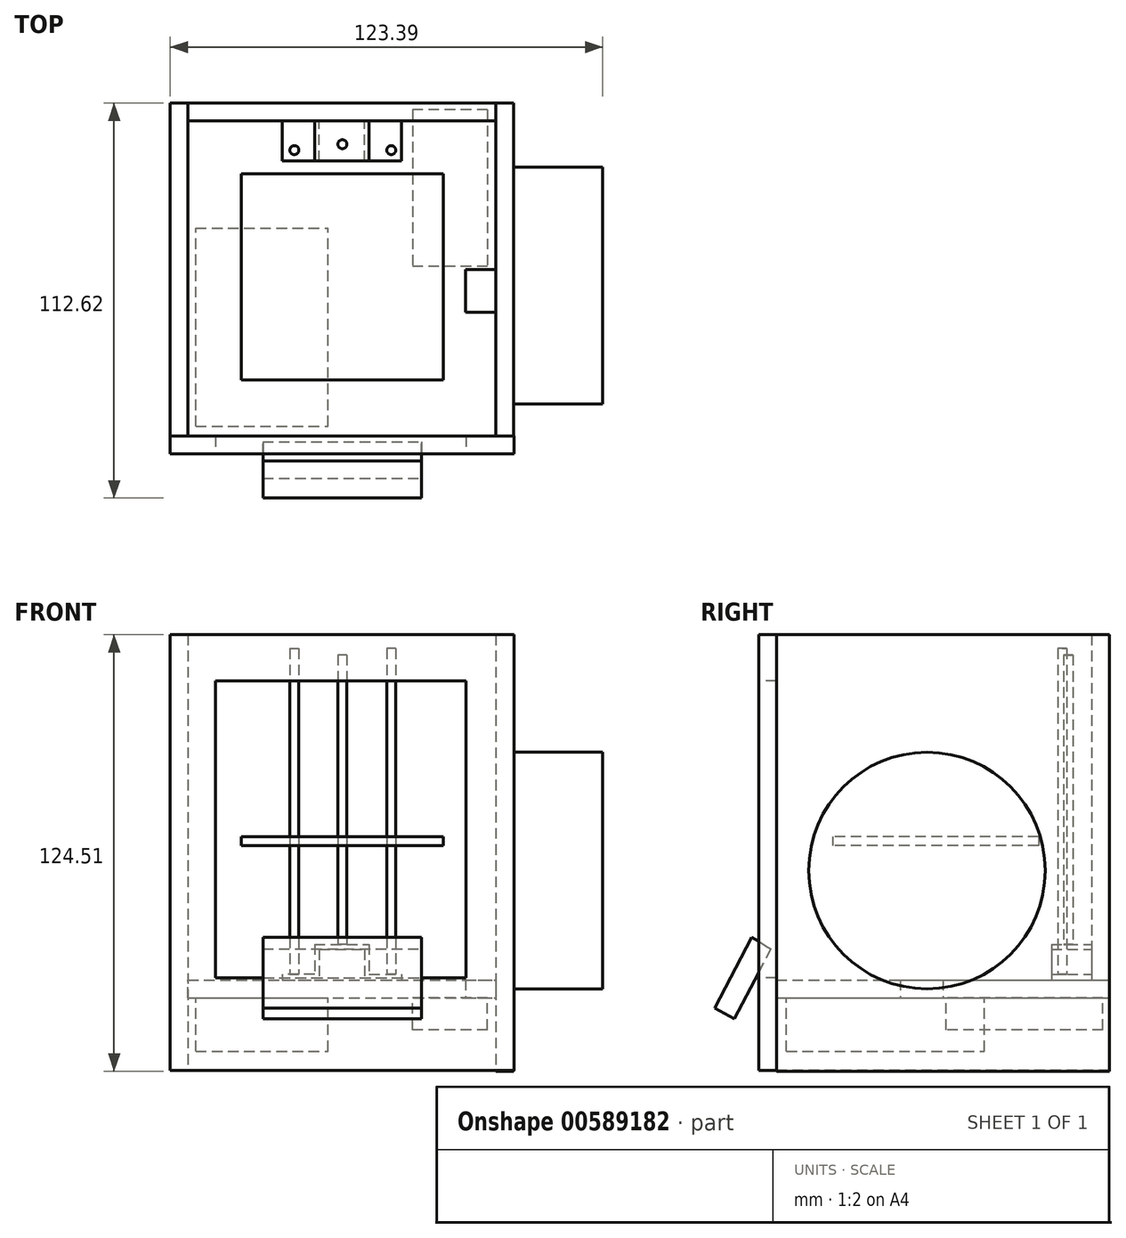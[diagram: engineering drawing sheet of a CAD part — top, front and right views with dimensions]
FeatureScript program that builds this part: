
annotation { "Feature Type Name" : "Feature", "Feature Type Description" : "" }
export const myFeature = defineFeature(function(context is Context, id is Id, definition is map)
    precondition{}
    {
        {
            var Q0;
            Q0=qCreatedBy(makeId("Front.planeOp"),FACE);
            var sketch = newSketch(context, id + "F0", { "sketchPlane" : qUnion([Q0])});
            skLineSegment(sketch, "E0.bottom", {"start": v(-50.38, 67.28) * mm, "end": v(37.45, 67.28) * mm});
            skLineSegment(sketch, "E0.top", {"start": v(-50.38, -31.18) * mm, "end": v(37.45, -31.18) * mm});
            skLineSegment(sketch, "E0.left", {"start": v(-50.38, 67.28) * mm, "end": v(-50.38, -31.18) * mm});
            skLineSegment(sketch, "E0.right", {"start": v(37.45, 67.28) * mm, "end": v(37.45, -31.18) * mm});
            skSolve(sketch);
        }
        {
            var Q0;
            Q0 = qSketchRegion(id + "F0", true);
            extrude(context, id + "F1", {"entities" : qUnion([Q0]), "depth" : 5.08 * mm, "offsetDistance" : 25.4 * mm});
        }
        {
            var Q0;
            Q0=makeQuery(id+"F1.opExtrude","SWEPT_FACE",FACE,{"disambiguationData":[OSD([sQuery(id+"F0.wireOp",EDGE,"E0.top")])]});
            var sketch = newSketch(context, id + "F2", { "sketchPlane" : qUnion([Q0])});
            skLineSegment(sketch, "E1.bottom", {"start": v(-50.38, 0) * mm, "end": v(37.45, 0) * mm});
            skLineSegment(sketch, "E1.top", {"start": v(-50.38, 95) * mm, "end": v(37.45, 95) * mm});
            skLineSegment(sketch, "E1.left", {"start": v(-50.38, 0) * mm, "end": v(-50.38, 95) * mm});
            skLineSegment(sketch, "E1.right", {"start": v(37.45, 0) * mm, "end": v(37.45, 95) * mm});
            skSolve(sketch);
        }
        {
            var Q0;
            Q0 = qSketchRegion(id + "F2", true);
            extrude(context, id + "F3", {"entities" : qUnion([Q0]), "depth" : 5.08 * mm, "offsetDistance" : 25.4 * mm});
        }
        {
            var Q0;
            Q0=makeQuery(id+"F3.boolean.opBoolean","MERGE",FACE,{"derivedFrom":[makeQuery(id+"F1.opExtrude","SWEPT_FACE",FACE,{"disambiguationData":[OSD([sQuery(id+"F0.wireOp",EDGE,"E0.right")])]}),makeQuery(id+"F3.opExtrude","SWEPT_FACE",FACE,{"disambiguationData":[OSD([sQuery(id+"F2.wireOp",EDGE,"E1.right")])]})]});
            var sketch = newSketch(context, id + "F4", { "sketchPlane" : qUnion([Q0])});
            skLineSegment(sketch, "E2.bottom", {"start": v(-95, 67.28) * mm, "end": v(0, 67.28) * mm});
            skLineSegment(sketch, "E2.top", {"start": v(-95, -57.23) * mm, "end": v(0, -57.23) * mm});
            skLineSegment(sketch, "E2.left", {"start": v(-95, 67.28) * mm, "end": v(-95, -57.23) * mm});
            skLineSegment(sketch, "E2.right", {"start": v(0, 67.28) * mm, "end": v(0, -57.23) * mm});
            skSolve(sketch);
        }
        {
            var Q0;
            Q0 = qSketchRegion(id + "F4", true);
            extrude(context, id + "F5", {"entities" : qUnion([Q0]), "depth" : 5.08 * mm, "offsetDistance" : 25.4 * mm});
        }
        {
            var Q0;
            Q0=makeQuery(id+"F3.boolean.opBoolean","MERGE",FACE,{"derivedFrom":[makeQuery(id+"F1.opExtrude","SWEPT_FACE",FACE,{"disambiguationData":[OSD([sQuery(id+"F0.wireOp",EDGE,"E0.left")])]}),makeQuery(id+"F3.opExtrude","SWEPT_FACE",FACE,{"disambiguationData":[OSD([sQuery(id+"F2.wireOp",EDGE,"E1.left")])]})]});
            var sketch = newSketch(context, id + "F6", { "sketchPlane" : qUnion([Q0])});
            skLineSegment(sketch, "E3.bottom", {"start": v(0, 67.28) * mm, "end": v(95, 67.28) * mm});
            skLineSegment(sketch, "E3.top", {"start": v(0, -56.96) * mm, "end": v(95, -56.96) * mm});
            skLineSegment(sketch, "E3.left", {"start": v(0, 67.28) * mm, "end": v(0, -56.96) * mm});
            skLineSegment(sketch, "E3.right", {"start": v(95, 67.28) * mm, "end": v(95, -56.96) * mm});
            skSolve(sketch);
        }
        {
            var Q0;
            Q0 = qSketchRegion(id + "F6", true);
            extrude(context, id + "F7", {"entities" : qUnion([Q0]), "depth" : 5.08 * mm, "offsetDistance" : 25.4 * mm});
        }
        {
            var Q0;
            Q0=makeQuery(id+"F7.opExtrude","SWEPT_FACE",FACE,{"disambiguationData":[OSD([sQuery(id+"F6.wireOp",EDGE,"E3.right")])]});
            var sketch = newSketch(context, id + "F8", { "sketchPlane" : qUnion([Q0])});
            skLineSegment(sketch, "E4.bottom", {"start": v(-55.46, 67.28) * mm, "end": v(42.63, 67.28) * mm});
            skLineSegment(sketch, "E4.top", {"start": v(-55.46, -56.96) * mm, "end": v(42.63, -56.96) * mm});
            skLineSegment(sketch, "E4.left", {"start": v(-55.46, 67.28) * mm, "end": v(-55.46, -56.96) * mm});
            skLineSegment(sketch, "E4.right", {"start": v(42.63, 67.28) * mm, "end": v(42.63, -56.96) * mm});
            skSolve(sketch);
        }
        {
            var Q0;
            Q0 = qSketchRegion(id + "F8", true);
            extrude(context, id + "F9", {"entities" : qUnion([Q0]), "depth" : 5.08 * mm, "offsetDistance" : 25.4 * mm});
        }
        {
            var Q0;
            Q0=makeQuery(id+"F9.opExtrude","CAP_FACE",FACE,{"disambiguationData":[OSD([sQuery(id+"F8.wireOp",EDGE,"E4.bottom"),sQuery(id+"F8.wireOp",EDGE,"E4.top"),sQuery(id+"F8.wireOp",EDGE,"E4.left"),sQuery(id+"F8.wireOp",EDGE,"E4.right")])],"isStart":false});
            var sketch = newSketch(context, id + "F10", { "sketchPlane" : qUnion([Q0])});
            skLineSegment(sketch, "E5.bottom", {"start": v(-42.59, -30.62) * mm, "end": v(28.93, -30.62) * mm});
            skLineSegment(sketch, "E5.top", {"start": v(-42.59, 54.13) * mm, "end": v(28.93, 54.13) * mm});
            skLineSegment(sketch, "E5.left", {"start": v(-42.59, -30.62) * mm, "end": v(-42.59, 54.13) * mm});
            skLineSegment(sketch, "E5.right", {"start": v(28.93, -30.62) * mm, "end": v(28.93, 54.13) * mm});
            skSolve(sketch);
        }
        {
            var Q0;
            Q0 = qSketchRegion(id + "F10", true);
            extrude(context, id + "F11", {"entities" : qUnion([Q0]), "operationType" : NewBodyOperationType.REMOVE, "oppositeDirection" : true, "depth" : 25.4 * mm, "offsetDistance" : 25.4 * mm});
        }
        {
            var Q0;
            Q0=makeQuery(id+"F1.opExtrude","CAP_FACE",FACE,{"disambiguationData":[OSD([sQuery(id+"F0.wireOp",EDGE,"E0.bottom"),sQuery(id+"F0.wireOp",EDGE,"E0.top"),sQuery(id+"F0.wireOp",EDGE,"E0.left"),sQuery(id+"F0.wireOp",EDGE,"E0.right")])],"isStart":false});
            var sketch = newSketch(context, id + "F12", { "sketchPlane" : qUnion([Q0])});
            skLineSegment(sketch, "E6", {"start": v(-6.47, -31.18) * mm, "end": v(-6.47, -22.57) * mm});
            skLineSegment(sketch, "E7", {"start": v(-6.47, -22.53) * mm, "end": v(0, -22.53) * mm});
            skLineSegment(sketch, "E8", {"start": v(0, -22.53) * mm, "end": v(0, -31.18) * mm});
            skLineSegment(sketch, "E9", {"start": v(-6.47, -21.06) * mm, "end": v(1.32, -21.06) * mm});
            skLineSegment(sketch, "E10", {"start": v(1.32, -21.06) * mm, "end": v(1.32, -29.66) * mm});
            skLineSegment(sketch, "E11", {"start": v(1.32, -29.66) * mm, "end": v(10.56, -29.66) * mm});
            skLineSegment(sketch, "E12", {"start": v(10.56, -29.66) * mm, "end": v(10.56, -31.18) * mm});
            skLineSegment(sketch, "E13", {"start": v(10.56, -31.18) * mm, "end": v(0, -31.18) * mm});
            skLineSegment(sketch, "E14.MirrorCS", {"start": v(-6.47, -21.06) * mm, "end": v(-14.25, -21.06) * mm});
            skLineSegment(sketch, "E15.MirrorCS", {"start": v(-6.47, -22.53) * mm, "end": v(-12.93, -22.53) * mm});
            skLineSegment(sketch, "E16.MirrorCS", {"start": v(-12.93, -22.53) * mm, "end": v(-12.93, -31.18) * mm});
            skLineSegment(sketch, "E17.MirrorCS", {"start": v(-14.25, -21.06) * mm, "end": v(-14.25, -29.66) * mm});
            skLineSegment(sketch, "E18.MirrorCS", {"start": v(-14.25, -29.66) * mm, "end": v(-23.5, -29.66) * mm});
            skLineSegment(sketch, "E19.MirrorCS", {"start": v(-23.5, -31.18) * mm, "end": v(-12.93, -31.18) * mm});
            skLineSegment(sketch, "E20.MirrorCS", {"start": v(-23.5, -29.66) * mm, "end": v(-23.5, -31.18) * mm});
            skSolve(sketch);
        }
        {
            var Q0;
            Q0 = qSketchRegion(id + "F12", true);
            extrude(context, id + "F13", {"entities" : qUnion([Q0]), "depth" : 11.43 * mm, "offsetDistance" : 25.4 * mm});
        }
        {
            var Q0;
            Q0=makeQuery(id+"F13.opExtrude","SWEPT_FACE",FACE,{"disambiguationData":[OSD([sQuery(id+"F12.wireOp",EDGE,"E9"),sQuery(id+"F12.wireOp",EDGE,"E14.MirrorCS")])]});
            var sketch = newSketch(context, id + "F14", { "sketchPlane" : qUnion([Q0])});
            skCircle(sketch, "E21", {"center": v(-6.3, -11.7) * mm, "radius": 1.29 * mm});
            skSolve(sketch);
        }
        {
            var Q0;
            Q0=makeQuery(id+"F13.opExtrude","SWEPT_FACE",FACE,{"disambiguationData":[OSD([sQuery(id+"F12.wireOp",EDGE,"E18.MirrorCS")])]});
            var sketch = newSketch(context, id + "F15", { "sketchPlane" : qUnion([Q0])});
            skCircle(sketch, "E22", {"center": v(-20.04, -13.39) * mm, "radius": 1.28 * mm});
            skCircle(sketch, "E23", {"center": v(7.62, -13.39) * mm, "radius": 1.28 * mm});
            skSolve(sketch);
        }
        {
            var Q0;
            Q0 = qSketchRegion(id + "F15", true);
            extrude(context, id + "F16", {"entities" : qUnion([Q0]), "operationType" : NewBodyOperationType.ADD, "depth" : 92.96 * mm, "offsetDistance" : 25.4 * mm});
        }
        {
            var Q0;
            Q0 = qSketchRegion(id + "F14", true);
            extrude(context, id + "F17", {"entities" : qUnion([Q0]), "depth" : 82.55 * mm, "offsetDistance" : 25.4 * mm});
        }
        {
            var Q0;
            Q0=makeQuery(id+"F3.opExtrude","CAP_FACE",FACE,{"disambiguationData":[OSD([sQuery(id+"F2.wireOp",EDGE,"E1.bottom"),sQuery(id+"F2.wireOp",EDGE,"E1.top"),sQuery(id+"F2.wireOp",EDGE,"E1.left"),sQuery(id+"F2.wireOp",EDGE,"E1.right")])],"isStart":false});
            var sketch = newSketch(context, id + "F18", { "sketchPlane" : qUnion([Q0])});
            skLineSegment(sketch, "E24.bottom", {"start": v(-48.16, 92.16) * mm, "end": v(-10.43, 92.16) * mm});
            skLineSegment(sketch, "E24.top", {"start": v(-48.16, 35.66) * mm, "end": v(-10.43, 35.66) * mm});
            skLineSegment(sketch, "E24.left", {"start": v(-48.16, 92.16) * mm, "end": v(-48.16, 35.66) * mm});
            skLineSegment(sketch, "E24.right", {"start": v(-10.43, 92.16) * mm, "end": v(-10.43, 35.66) * mm});
            skSolve(sketch);
        }
        {
            var Q0;
            Q0=makeQuery(id+"F18.imprint","IMPRINT",FACE,{"disambiguationData":[TD([[makeQuery(id+"F18.imprint","IMPRINT",EDGE,{"derivedFrom":sQuery(id+"F18.wireOp",EDGE,"E24.bottom")}),-1.0]])]});
            extrude(context, id + "F19", {"entities" : qUnion([Q0]), "depth" : 15.24 * mm, "offsetDistance" : 25.4 * mm});
        }
        {
            var Q0;
            Q0=makeQuery(id+"F3.opExtrude","CAP_FACE",FACE,{"disambiguationData":[OSD([sQuery(id+"F2.wireOp",EDGE,"E1.bottom"),sQuery(id+"F2.wireOp",EDGE,"E1.top"),sQuery(id+"F2.wireOp",EDGE,"E1.left"),sQuery(id+"F2.wireOp",EDGE,"E1.right")])],"isStart":false});
            var sketch = newSketch(context, id + "F20", { "sketchPlane" : qUnion([Q0])});
            skLineSegment(sketch, "E25.bottom", {"start": v(35.07, 1.84) * mm, "end": v(13.73, 1.84) * mm});
            skLineSegment(sketch, "E25.top", {"start": v(35.07, 46.5) * mm, "end": v(13.73, 46.5) * mm});
            skLineSegment(sketch, "E25.left", {"start": v(35.07, 1.84) * mm, "end": v(35.07, 46.5) * mm});
            skLineSegment(sketch, "E25.right", {"start": v(13.73, 1.84) * mm, "end": v(13.73, 46.5) * mm});
            skSolve(sketch);
        }
        {
            var Q0;
            Q0=makeQuery(id+"F20.imprint","IMPRINT",FACE,{"disambiguationData":[TD([[makeQuery(id+"F20.imprint","IMPRINT",EDGE,{"derivedFrom":sQuery(id+"F20.wireOp",EDGE,"E25.bottom")}),-1.0]])]});
            extrude(context, id + "F21", {"entities" : qUnion([Q0]), "depth" : 9.14 * mm, "offsetDistance" : 25.4 * mm});
        }
        {
            var Q0;
            Q0=makeQuery(id+"F3.opExtrude","CAP_FACE",FACE,{"disambiguationData":[OSD([sQuery(id+"F2.wireOp",EDGE,"E1.bottom"),sQuery(id+"F2.wireOp",EDGE,"E1.top"),sQuery(id+"F2.wireOp",EDGE,"E1.left"),sQuery(id+"F2.wireOp",EDGE,"E1.right")])],"isStart":false});
            var sketch = newSketch(context, id + "F22", { "sketchPlane" : qUnion([Q0])});
            skLineSegment(sketch, "E26.bottom", {"start": v(28.88, 59.65) * mm, "end": v(37.45, 59.65) * mm});
            skLineSegment(sketch, "E26.top", {"start": v(28.88, 47.5) * mm, "end": v(37.45, 47.5) * mm});
            skLineSegment(sketch, "E26.left", {"start": v(28.88, 59.65) * mm, "end": v(28.88, 47.5) * mm});
            skLineSegment(sketch, "E26.right", {"start": v(37.45, 59.65) * mm, "end": v(37.45, 47.5) * mm});
            skSolve(sketch);
        }
        {
            var Q0;
            Q0=makeQuery(id+"F22.imprint","IMPRINT",FACE,{"disambiguationData":[TD([[makeQuery(id+"F22.imprint","IMPRINT",EDGE,{"derivedFrom":sQuery(id+"F22.wireOp",EDGE,"E26.bottom")}),-1.0]])]});
            extrude(context, id + "F23", {"entities" : qUnion([Q0]), "operationType" : NewBodyOperationType.REMOVE, "oppositeDirection" : true, "depth" : 25.4 * mm, "offsetDistance" : 25.4 * mm});
        }
        {
            var Q0;
            Q0=makeQuery(id+"F3.opExtrude","CAP_FACE",FACE,{"disambiguationData":[OSD([sQuery(id+"F2.wireOp",EDGE,"E1.bottom"),sQuery(id+"F2.wireOp",EDGE,"E1.top"),sQuery(id+"F2.wireOp",EDGE,"E1.left"),sQuery(id+"F2.wireOp",EDGE,"E1.right")])],"isStart":true});
            cPlane(context, id + "F24", {"entities" : qUnion([Q0]), "cplaneType" : CPlaneType.OFFSET, "offset" : 38.35 * mm, "width" : 152.4 * mm, "height" : 152.4 * mm});
        }
        {
            var Q0;
            Q0=qCreatedBy(id+"F24.planeOp",FACE);
            var sketch = newSketch(context, id + "F25", { "sketchPlane" : qUnion([Q0])});
            skLineSegment(sketch, "E27.bottom", {"start": v(-35.16, -20.16) * mm, "end": v(22.45, -20.16) * mm});
            skLineSegment(sketch, "E27.top", {"start": v(-35.16, -78.9) * mm, "end": v(22.45, -78.9) * mm});
            skLineSegment(sketch, "E27.left", {"start": v(-35.16, -20.16) * mm, "end": v(-35.16, -78.9) * mm});
            skLineSegment(sketch, "E27.right", {"start": v(22.45, -20.16) * mm, "end": v(22.45, -78.9) * mm});
            skSolve(sketch);
        }
        {
            var Q0;
            Q0=makeQuery(id+"F25.imprint","IMPRINT",FACE,{"disambiguationData":[TD([[makeQuery(id+"F25.imprint","IMPRINT",EDGE,{"derivedFrom":sQuery(id+"F25.wireOp",EDGE,"E27.bottom")}),-1.0]])]});
            extrude(context, id + "F26", {"entities" : qUnion([Q0]), "depth" : 2.54 * mm, "offsetDistance" : 25.4 * mm});
        }
        {
            var Q0;
            Q0=makeQuery(id+"F9.opExtrude","SWEPT_FACE",FACE,{"disambiguationData":[OSD([sQuery(id+"F8.wireOp",EDGE,"E4.right")])]});
            cPlane(context, id + "F27", {"entities" : qUnion([Q0]), "cplaneType" : CPlaneType.OFFSET, "offset" : 26.42 * mm, "oppositeDirection" : true, "width" : 152.4 * mm, "height" : 152.4 * mm});
        }
        {
            var Q0;
            Q0=qCreatedBy(id+"F27.planeOp",FACE);
            var sketch = newSketch(context, id + "F28", { "sketchPlane" : qUnion([Q0])});
            skLineSegment(sketch, "E28", {"start": v(-96.58, -22.39) * mm, "end": v(-106.95, -42.24) * mm});
            skLineSegment(sketch, "E29", {"start": v(-106.95, -42.24) * mm, "end": v(-112.62, -39.28) * mm});
            skLineSegment(sketch, "E30", {"start": v(-112.62, -39.28) * mm, "end": v(-102.06, -19.05) * mm});
            skLineSegment(sketch, "E31", {"start": v(-102.06, -19.05) * mm, "end": v(-96.58, -22.39) * mm});
            skSolve(sketch);
        }
        {
            var Q0;
            Q0 = qSketchRegion(id + "F28", true);
            extrude(context, id + "F29", {"entities" : qUnion([Q0]), "oppositeDirection" : true, "depth" : 45.2 * mm, "offsetDistance" : 25.4 * mm});
        }
        {
            var Q0;
            Q0=makeQuery(id+"F5.opExtrude","CAP_FACE",FACE,{"disambiguationData":[OSD([sQuery(id+"F4.wireOp",EDGE,"E2.bottom"),sQuery(id+"F4.wireOp",EDGE,"E2.top"),sQuery(id+"F4.wireOp",EDGE,"E2.left"),sQuery(id+"F4.wireOp",EDGE,"E2.right")])],"isStart":false});
            var sketch = newSketch(context, id + "F30", { "sketchPlane" : qUnion([Q0])});
            skCircle(sketch, "E32", {"center": v(-52.01, 0) * mm, "radius": 33.74 * mm});
            skSolve(sketch);
        }
        {
            var Q0;
            Q0=makeQuery(id+"F30.imprint","IMPRINT",FACE,{"disambiguationData":[TD([[makeQuery(id+"F30.imprint","IMPRINT",EDGE,{"derivedFrom":sQuery(id+"F30.wireOp",EDGE,"E32")}),1.0]])]});
            extrude(context, id + "F31", {"entities" : qUnion([Q0]), "depth" : 25.4 * mm, "offsetDistance" : 25.4 * mm});
        }
    });
